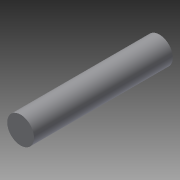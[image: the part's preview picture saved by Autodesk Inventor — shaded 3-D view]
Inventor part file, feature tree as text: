
AUTODESK INVENTOR PART (.ipt)
format: ipt  version: 2015 (Build 190159000, 159)  size: 69,632 bytes
history: native  units: mm
features: extrude x1, sketch x1
ambient origin geometry x8: Origin, YZ Plane, XZ Plane, XY Plane, X Axis, Y Axis, Z Axis, Center Point
bodies: Solid1 (feature_tree)
feature tree (2):
  extrude  "Extrusion1"  Depth=15.0mm
  sketch  "Sketch1"  dims[d1=15.0mm d2=0.0mm d6=2.9mm]
